# Revit family: Hand_Shower-GROHE-SmartActive-26545_Series
name_source: partatom
category: Plumbing Fixtures
revit_build: Autodesk Revit 2016 (Build: 20150714_1515(x64)
units: mm (PartAtom-declared; Revit-internal decimal feet)

## family parameters
Always vertical = No
Cut with Voids When Loaded = No
OmniClass Number = 23.45.05.14.17
OmniClass Title = Showers
Part Type = Normal
Room Calculation Point = No
Round Connector Dimension = Use Diameter
Shared = Yes
Work Plane-Based = Yes

## types (5) — shared parameters
Assembly Code = D2010710
CW Connection = Yes
CWFU = 3
CalGreen Compliant = Yes
Cold Water Connection Diameter = 1/2"
Cold Water Connection Radius = 1/4"
Default Elevation = 0"
Description = Rainshower SmartActive Hand Shower - 3 Sprays, 1.75 GPM
Flow Rate = 1.75 gpm (6.6 L/min)
HW Connection = Yes
HWFU = 3
Height = 6 15/16"
Hot Water Connection Diameter = 1"
Hot Water Connection Radius = 1/4"
Manufacturer = Grohe
Price = Prices may vary. Please consult Manufacturer Representative for most up-to-date price list.
Tempered Connection Diameter = 1/2"
Tempered Connection Radius = 1/4"
URL = https://www.grohe.us
Vent Connection = No
WFU = 4
Warranty Documentation Link = https://cdn.cloud.grohe.com
Waste Connection = No
cUPC Compliant = Yes

## per-type parameters (varying)
| type | Finish | Material |
| 26545000 | Grohe-000-StarLight Chrome | Grohe-000-StarLight Chrome |
| 26545EN0 | Grohe-EN0-Brushed Nickel InfinityFinish | Grohe-EN0-Brushed Nickel InfinityFinish |
| 26545GN0 | Grohe-GN0-Brushed Cool Sunrise | Grohe-GN0-Brushed Cool Sunrise |
| 26545A00 | Grohe-A00-Hard Graphite | Grohe-A00-Hard Graphite |
| 26545BE0 | Grohe-BE0-Polished Nickel InfinityFinish | Grohe-BE0-Polished Nickel InfinityFinish |

note: column(s) folded — value = type name in every type: Model

## geometry (parser evidence)
native form markers: Sweep x2
no freeform markers — native parametric forms only
